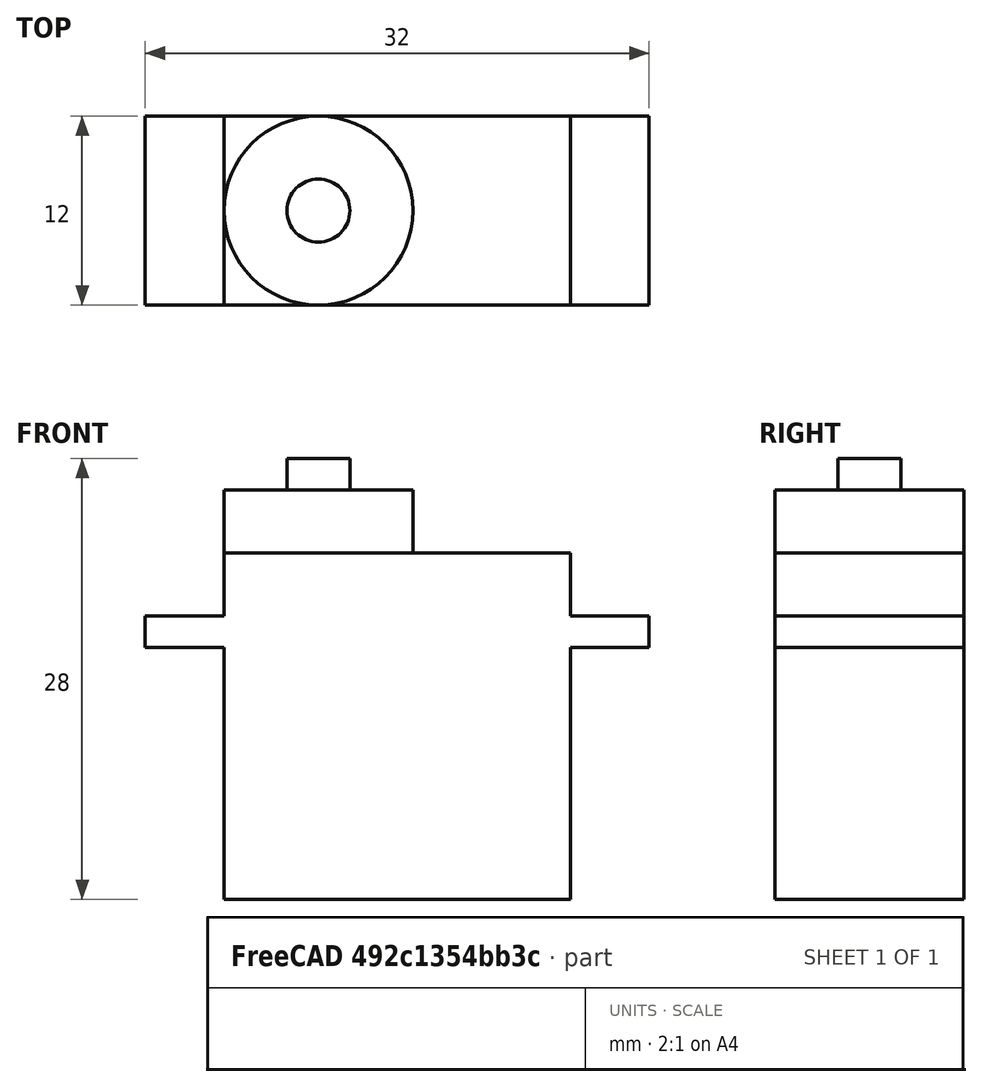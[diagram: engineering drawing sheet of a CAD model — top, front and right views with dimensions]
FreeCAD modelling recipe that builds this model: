
FCSTD DOCUMENT  (FreeCAD 0.18R16131 (Git))
Label: servo
License: All rights reserved
LicenseURL: http://en.wikipedia.org/wiki/All_rights_reserved
objects: Part::Box×2, Part::Cylinder×2, Part::MultiFuse×1
note: 5 computed .brp shape members not serialized (recipe doc carries the construction recipe); baked Part::Feature solids carry a one-line shape summary decoded from their .brp

FEATURE [Part::Box] Box  label="Cube"
  AttacherType = Attacher::AttachEngine3D
  Height = 22
  Length = 22
  Width = 12
FEATURE [Part::Box] Box001  label="Cube001"
  AttacherType = Attacher::AttachEngine3D
  Height = 2
  Length = 32
  Placement = pos=(-5,0,16) rot=(0,0,1;0rad)
  Width = 12
FEATURE [Part::Cylinder] Cylinder
  Angle = 360
  AttacherType = Attacher::AttachEngine3D
  Height = 4
  Placement = pos=(6,6,22) rot=(0,0,1;0rad)
  Radius = 6
FEATURE [Part::Cylinder] Cylinder001
  Angle = 360
  AttacherType = Attacher::AttachEngine3D
  Height = 2
  Placement = pos=(6,6,26) rot=(0,0,1;0rad)
  Radius = 2
FEATURE [Part::MultiFuse] Fusion
  Shapes = -> [Cylinder,Box,Box001,Cylinder001]
